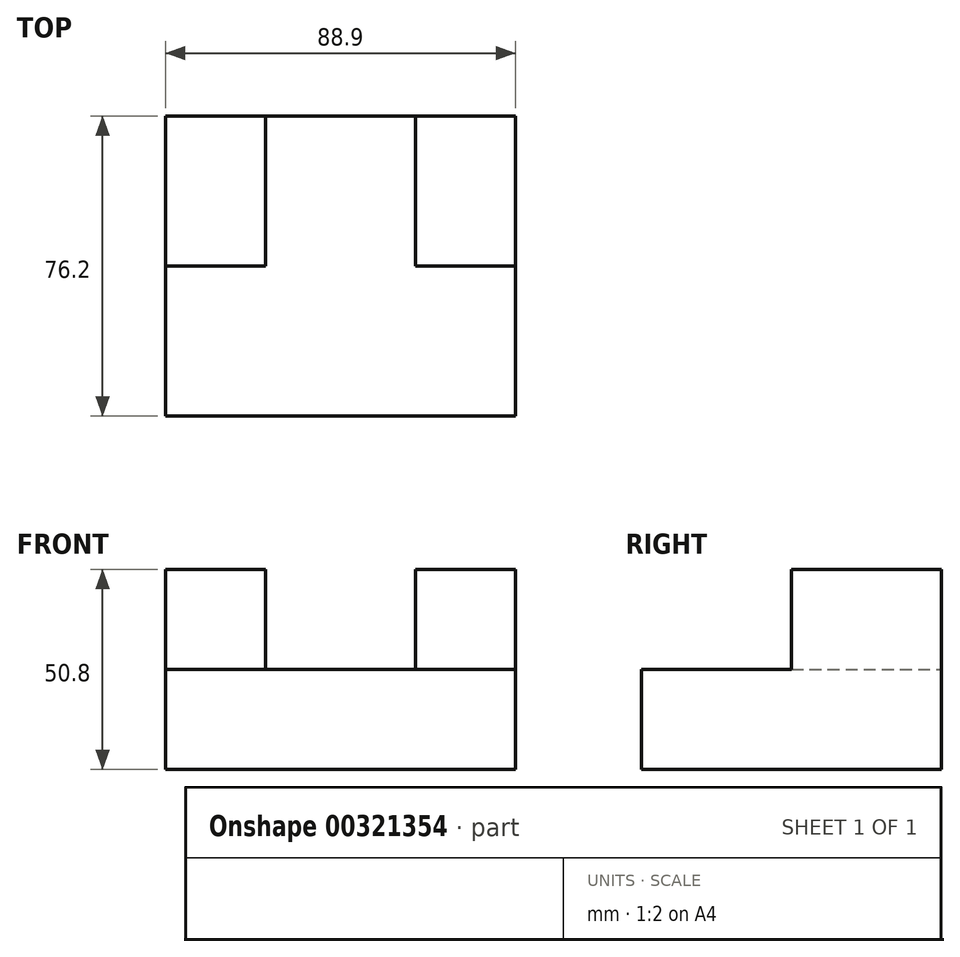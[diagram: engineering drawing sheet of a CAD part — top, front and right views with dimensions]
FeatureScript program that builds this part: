
annotation { "Feature Type Name" : "Feature", "Feature Type Description" : "" }
export const myFeature = defineFeature(function(context is Context, id is Id, definition is map)
    precondition{}
    {
        {
            var Q0;
            Q0=qCreatedBy(makeId("Right.planeOp"),FACE);
            var sketch = newSketch(context, id + "F0", { "sketchPlane" : qUnion([Q0])});
            skLineSegment(sketch, "E0", {"start": v(-25.55, -28.42) * mm, "end": v(50.65, -28.42) * mm});
            skLineSegment(sketch, "E1", {"start": v(50.65, -28.42) * mm, "end": v(50.65, 22.38) * mm});
            skLineSegment(sketch, "E2", {"start": v(50.65, 22.38) * mm, "end": v(12.55, 22.38) * mm});
            skLineSegment(sketch, "E3", {"start": v(12.55, 22.38) * mm, "end": v(12.55, -3.02) * mm});
            skLineSegment(sketch, "E4", {"start": v(12.55, -3.02) * mm, "end": v(-25.55, -3.02) * mm});
            skLineSegment(sketch, "E5", {"start": v(-25.55, -3.02) * mm, "end": v(-25.55, -28.42) * mm});
            skSolve(sketch);
        }
        {
            var Q0;
            Q0=makeQuery(id+"F0.imprint","IMPRINT",FACE,{"disambiguationData":[TD([[makeQuery(id+"F0.imprint","IMPRINT",EDGE,{"derivedFrom":sQuery(id+"F0.wireOp",EDGE,"E0")}),1.0]])]});
            extrude(context, id + "F1", {"entities" : qUnion([Q0]), "depth" : 88.9 * mm});
        }
        {
            var Q0;
            Q0=makeQuery(id+"F1.opExtrude","SWEPT_FACE",FACE,{"disambiguationData":[OSD([sQuery(id+"F0.wireOp",EDGE,"E2")])]});
            var sketch = newSketch(context, id + "F2", { "sketchPlane" : qUnion([Q0])});
            skLineSegment(sketch, "E6", {"start": v(63.5, 12.55) * mm, "end": v(63.5, 50.65) * mm});
            skLineSegment(sketch, "E7", {"start": v(25.4, 12.55) * mm, "end": v(25.4, 50.65) * mm});
            skSolve(sketch);
        }
        {
            var Q0;
            Q0 = qSketchRegion(id + "F2", true);
            var Q1;
            {var subQ0=sQuery(id+"F2.wireOp",EDGE,"E6");Q1=makeQuery(id+"F2.imprint","IMPRINT",FACE,{"disambiguationData":[TD([[makeQuery(id+"F2.imprint","IMPRINT",EDGE,{"derivedFrom":subQ0}),1.0]])]});}
            extrude(context, id + "F3", {"entities" : qUnion([Q0, Q1]), "operationType" : NewBodyOperationType.REMOVE, "oppositeDirection" : true, "depth" : 25.4 * mm});
        }
    });
